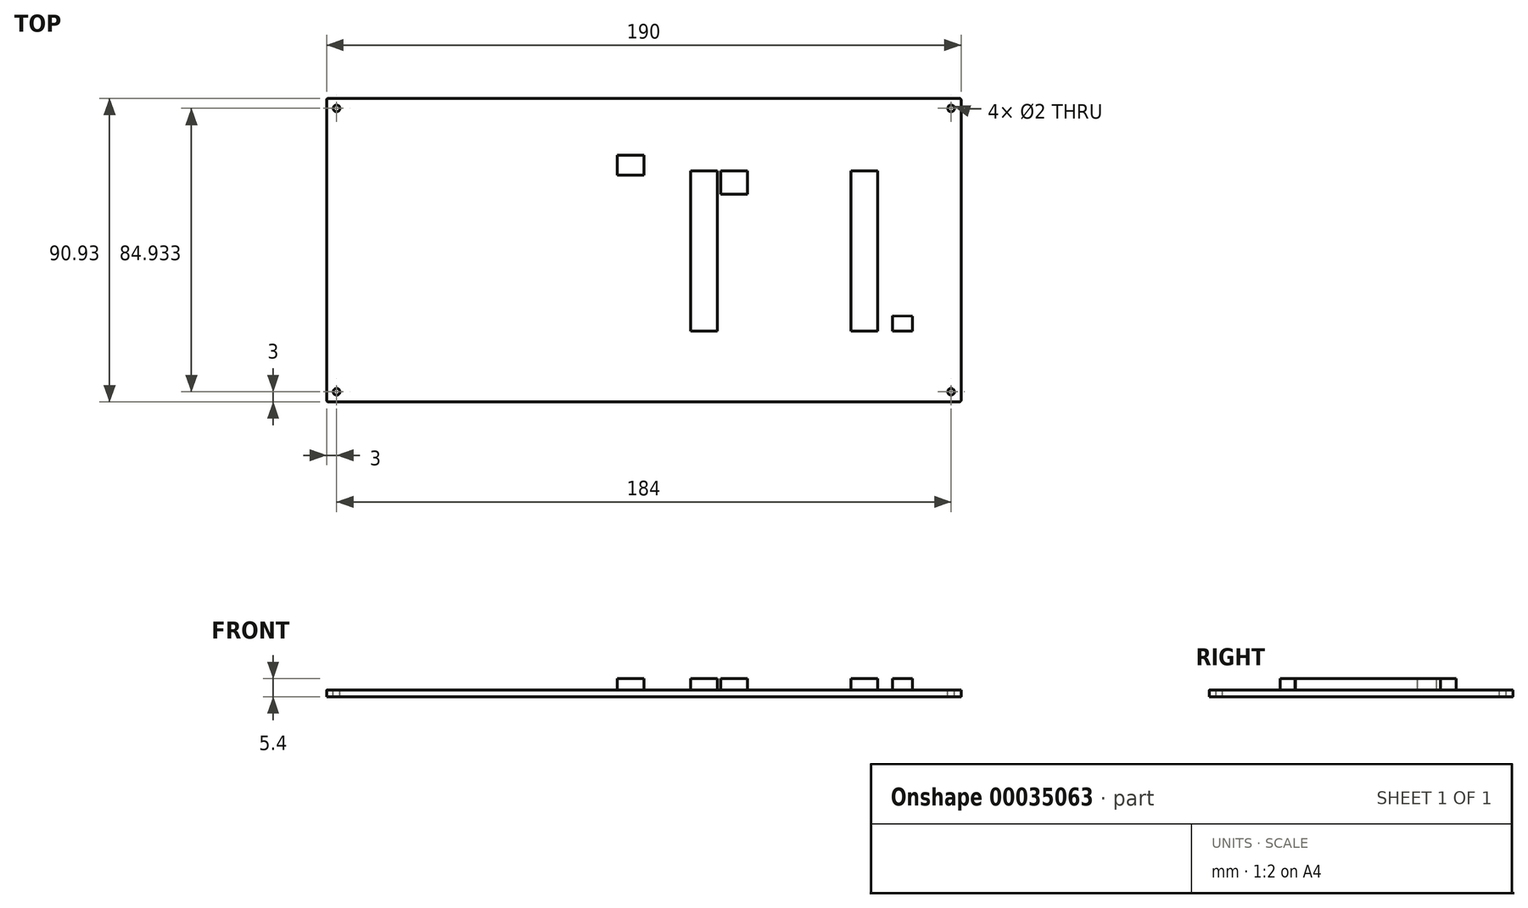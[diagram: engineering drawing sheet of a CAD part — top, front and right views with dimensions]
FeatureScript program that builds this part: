
annotation { "Feature Type Name" : "Feature", "Feature Type Description" : "" }
export const myFeature = defineFeature(function(context is Context, id is Id, definition is map)
    precondition{}
    {
        {
            var Q0;
            Q0=qCreatedBy(makeId("Top.planeOp"),FACE);
            var sketch = newSketch(context, id + "F0", { "sketchPlane" : qUnion([Q0])});
            skLineSegment(sketch, "E0.bottom", {"start": v(0, 0) * mm, "end": v(190, 0) * mm});
            skLineSegment(sketch, "E0.top", {"start": v(0, 90.93) * mm, "end": v(190, 90.93) * mm});
            skLineSegment(sketch, "E0.left", {"start": v(0, 0) * mm, "end": v(0, 90.93) * mm});
            skLineSegment(sketch, "E0.right", {"start": v(190, 0) * mm, "end": v(190, 90.93) * mm});
            skSolve(sketch);
        }
        {
            var Q0;
            Q0 = qSketchRegion(id + "F0", true);
            extrude(context, id + "F1", {"entities" : qUnion([Q0]), "depth" : 2 * mm});
        }
        {
            var Q0;
            Q0=makeQuery(id+"F1.opExtrude","CAP_FACE",FACE,{"disambiguationData":[OSD([sQuery(id+"F0.wireOp",EDGE,"E0.bottom"),sQuery(id+"F0.wireOp",EDGE,"E0.top"),sQuery(id+"F0.wireOp",EDGE,"E0.left"),sQuery(id+"F0.wireOp",EDGE,"E0.right")])],"isStart":false});
            var sketch = newSketch(context, id + "F2", { "sketchPlane" : qUnion([Q0])});
            skCircle(sketch, "E1", {"center": v(3, 87.93) * mm, "radius": 1 * mm});
            skCircle(sketch, "E2", {"center": v(3, 3) * mm, "radius": 1 * mm});
            skSolve(sketch);
        }
        {
            var Q0;
            Q0=makeQuery(id+"F2.imprint","IMPRINT",FACE,{"disambiguationData":[TD([[makeQuery(id+"F2.imprint","IMPRINT",EDGE,{"derivedFrom":sQuery(id+"F2.wireOp",EDGE,"E1")}),1.0]])]});
            var Q1;
            Q1=makeQuery(id+"F2.imprint","IMPRINT",FACE,{"disambiguationData":[TD([[makeQuery(id+"F2.imprint","IMPRINT",EDGE,{"derivedFrom":sQuery(id+"F2.wireOp",EDGE,"E2")}),1.0]])]});
            extrude(context, id + "F3", {"entities" : qUnion([Q0, Q1]), "operationType" : NewBodyOperationType.REMOVE, "endBound" : BoundingType.THROUGH_ALL, "oppositeDirection" : true, "depth" : 2 * mm});
        }
        {
            var Q0;
            Q0=makeQuery(id+"F1.opExtrude","SWEPT_FACE",FACE,{"disambiguationData":[OSD([sQuery(id+"F0.wireOp",EDGE,"E0.left")])]});
            cPlane(context, id + "F4", {"entities" : qUnion([Q0]), "cplaneType" : CPlaneType.OFFSET, "offset" : (190 / 2) * mm, "oppositeDirection" : true, "width" : 150 * mm, "height" : 150 * mm});
        }
        {
            var Q0;
            Q0=makeQuery(id+"F3.boolean.opBoolean","COPY",FACE,{"derivedFrom":makeQuery(id+"F3.opExtrude","SWEPT_FACE",FACE,{"disambiguationData":[OSD([sQuery(id+"F2.wireOp",EDGE,"E1")])]})});
            var Q1;
            Q1=makeQuery(id+"F3.boolean.opBoolean","COPY",FACE,{"derivedFrom":makeQuery(id+"F3.opExtrude","SWEPT_FACE",FACE,{"disambiguationData":[OSD([sQuery(id+"F2.wireOp",EDGE,"E2")])]})});
            var Q2;
            Q2=qCreatedBy(id+"F4.planeOp",FACE);
            mirror(context, id + "F5", {"faces" : qUnion([Q0, Q1]), "mirrorPlane" : qUnion([Q2]), "patternType" : MirrorType.FACE});
        }
        {
            var Q0;
            Q0=makeQuery(id+"F1.opExtrude","SWEPT_EDGE",EDGE,{"disambiguationData":[OSD([sQuery(id+"F0.wireOp",EDGE,"E0.bottom"),sQuery(id+"F0.wireOp",EDGE,"E0.right")])]});
            var Q1;
            Q1=makeQuery(id+"F1.opExtrude","SWEPT_EDGE",EDGE,{"disambiguationData":[OSD([sQuery(id+"F0.wireOp",EDGE,"E0.top"),sQuery(id+"F0.wireOp",EDGE,"E0.right")])]});
            var Q2;
            Q2=makeQuery(id+"F1.opExtrude","SWEPT_EDGE",EDGE,{"disambiguationData":[OSD([sQuery(id+"F0.wireOp",EDGE,"E0.top"),sQuery(id+"F0.wireOp",EDGE,"E0.left")])]});
            var Q3;
            Q3=makeQuery(id+"F1.opExtrude","SWEPT_EDGE",EDGE,{"disambiguationData":[OSD([sQuery(id+"F0.wireOp",EDGE,"E0.bottom"),sQuery(id+"F0.wireOp",EDGE,"E0.left")])]});
            fillet(context, id + "F6", {"entities" : qUnion([Q0, Q1, Q2, Q3]), "radius" : 0.5 * mm, "tangentPropagation" : true, "allowEdgeOverflow" : false});
        }
        {
            var Q0;
            Q0=makeQuery(id+"F1.opExtrude","CAP_FACE",FACE,{"disambiguationData":[OSD([sQuery(id+"F0.wireOp",EDGE,"E0.bottom"),sQuery(id+"F0.wireOp",EDGE,"E0.top"),sQuery(id+"F0.wireOp",EDGE,"E0.left"),sQuery(id+"F0.wireOp",EDGE,"E0.right")])],"isStart":false});
            var sketch = newSketch(context, id + "F7", { "sketchPlane" : qUnion([Q0])});
            skLineSegment(sketch, "E3.bottom", {"start": v(109, 69.23) * mm, "end": v(117, 69.23) * mm});
            skLineSegment(sketch, "E3.top", {"start": v(109, 21.23) * mm, "end": v(117, 21.23) * mm});
            skLineSegment(sketch, "E3.left", {"start": v(109, 69.23) * mm, "end": v(109, 21.23) * mm});
            skLineSegment(sketch, "E3.right", {"start": v(117, 69.23) * mm, "end": v(117, 21.23) * mm});
            skLineSegment(sketch, "E4.bottom", {"start": v(157, 69.23) * mm, "end": v(165, 69.23) * mm});
            skLineSegment(sketch, "E4.top", {"start": v(157, 21.23) * mm, "end": v(165, 21.23) * mm});
            skLineSegment(sketch, "E4.left", {"start": v(157, 69.23) * mm, "end": v(157, 21.23) * mm});
            skLineSegment(sketch, "E5.bottom", {"start": v(76.9, 86.6) * mm, "end": v(88.4, 86.6) * mm});
            skLineSegment(sketch, "E5.top", {"start": v(76.9, 78.7) * mm, "end": v(88.4, 78.7) * mm});
            skLineSegment(sketch, "E5.left", {"start": v(76.9, 86.6) * mm, "end": v(76.9, 78.7) * mm});
            skLineSegment(sketch, "E5.right", {"start": v(88.4, 86.6) * mm, "end": v(88.4, 78.7) * mm});
            skLineSegment(sketch, "E6.bottom", {"start": v(118, 62.23) * mm, "end": v(126, 62.23) * mm});
            skLineSegment(sketch, "E6.top", {"start": v(118, 69.23) * mm, "end": v(126, 69.23) * mm});
            skLineSegment(sketch, "E6.left", {"start": v(118, 69.23) * mm, "end": v(118, 62.23) * mm});
            skLineSegment(sketch, "E6.right", {"start": v(126, 69.23) * mm, "end": v(126, 62.23) * mm});
            skLineSegment(sketch, "E7.right", {"start": v(169.43, 21.25) * mm, "end": v(169.43, 25.75) * mm});
            skLineSegment(sketch, "E8", {"start": v(165, 69.23) * mm, "end": v(165, 21.23) * mm});
            skLineSegment(sketch, "E9", {"start": v(169.43, 21.25) * mm, "end": v(175.43, 21.25) * mm});
            skLineSegment(sketch, "E10", {"start": v(175.43, 21.25) * mm, "end": v(175.43, 25.7) * mm});
            skLineSegment(sketch, "E11", {"start": v(175.43, 25.7) * mm, "end": v(169.43, 25.75) * mm});
            skSolve(sketch);
        }
        {
            var Q0;
            Q0=makeQuery(id+"F7.imprint","IMPRINT",FACE,{"disambiguationData":[TD([[makeQuery(id+"F7.imprint","IMPRINT",EDGE,{"derivedFrom":sQuery(id+"F7.wireOp",EDGE,"E3.bottom")}),-1.0]])]});
            var Q1;
            Q1=makeQuery(id+"F7.imprint","IMPRINT",FACE,{"disambiguationData":[TD([[makeQuery(id+"F7.imprint","IMPRINT",EDGE,{"derivedFrom":sQuery(id+"F7.wireOp",EDGE,"E4.bottom")}),-1.0]])]});
            var Q2;
            Q2=makeQuery(id+"F7.imprint","IMPRINT",FACE,{"disambiguationData":[TD([[makeQuery(id+"F7.imprint","IMPRINT",EDGE,{"derivedFrom":sQuery(id+"F7.wireOp",EDGE,"E6.bottom")}),1.0]])]});
            var Q3;
            Q3=makeQuery(id+"F7.imprint","IMPRINT",FACE,{"disambiguationData":[TD([[makeQuery(id+"F7.imprint","IMPRINT",EDGE,{"derivedFrom":sQuery(id+"F7.wireOp",EDGE,"E7.bottom")}),1.0]])]});
            var Q4;
            Q4=makeQuery(id+"F7.imprint","IMPRINT",FACE,{"disambiguationData":[TD([[makeQuery(id+"F7.imprint","IMPRINT",EDGE,{"derivedFrom":sQuery(id+"F7.wireOp",EDGE,"E7.right")}),-1.0]])]});
            extrude(context, id + "F8", {"entities" : qUnion([Q0, Q1, Q2, Q3, Q4]), "operationType" : NewBodyOperationType.ADD, "depth" : 3.4 * mm});
        }
        {
            var Q0;
            Q0=makeQuery(id+"F1.opExtrude","CAP_FACE",FACE,{"disambiguationData":[OSD([sQuery(id+"F0.wireOp",EDGE,"E0.bottom"),sQuery(id+"F0.wireOp",EDGE,"E0.top"),sQuery(id+"F0.wireOp",EDGE,"E0.left"),sQuery(id+"F0.wireOp",EDGE,"E0.right")])],"isStart":false});
            var sketch = newSketch(context, id + "F9", { "sketchPlane" : qUnion([Q0])});
            skLineSegment(sketch, "E12.bottom", {"start": v(87, 73.93) * mm, "end": v(95, 73.93) * mm});
            skLineSegment(sketch, "E12.top", {"start": v(87, 67.93) * mm, "end": v(95, 67.93) * mm});
            skLineSegment(sketch, "E12.left", {"start": v(87, 73.93) * mm, "end": v(87, 67.93) * mm});
            skLineSegment(sketch, "E12.right", {"start": v(95, 73.93) * mm, "end": v(95, 67.93) * mm});
            skSolve(sketch);
        }
        {
            var Q0;
            Q0 = qSketchRegion(id + "F9", true);
            extrude(context, id + "F10", {"entities" : qUnion([Q0]), "operationType" : NewBodyOperationType.ADD, "depth" : 3.4 * mm});
        }
    });
